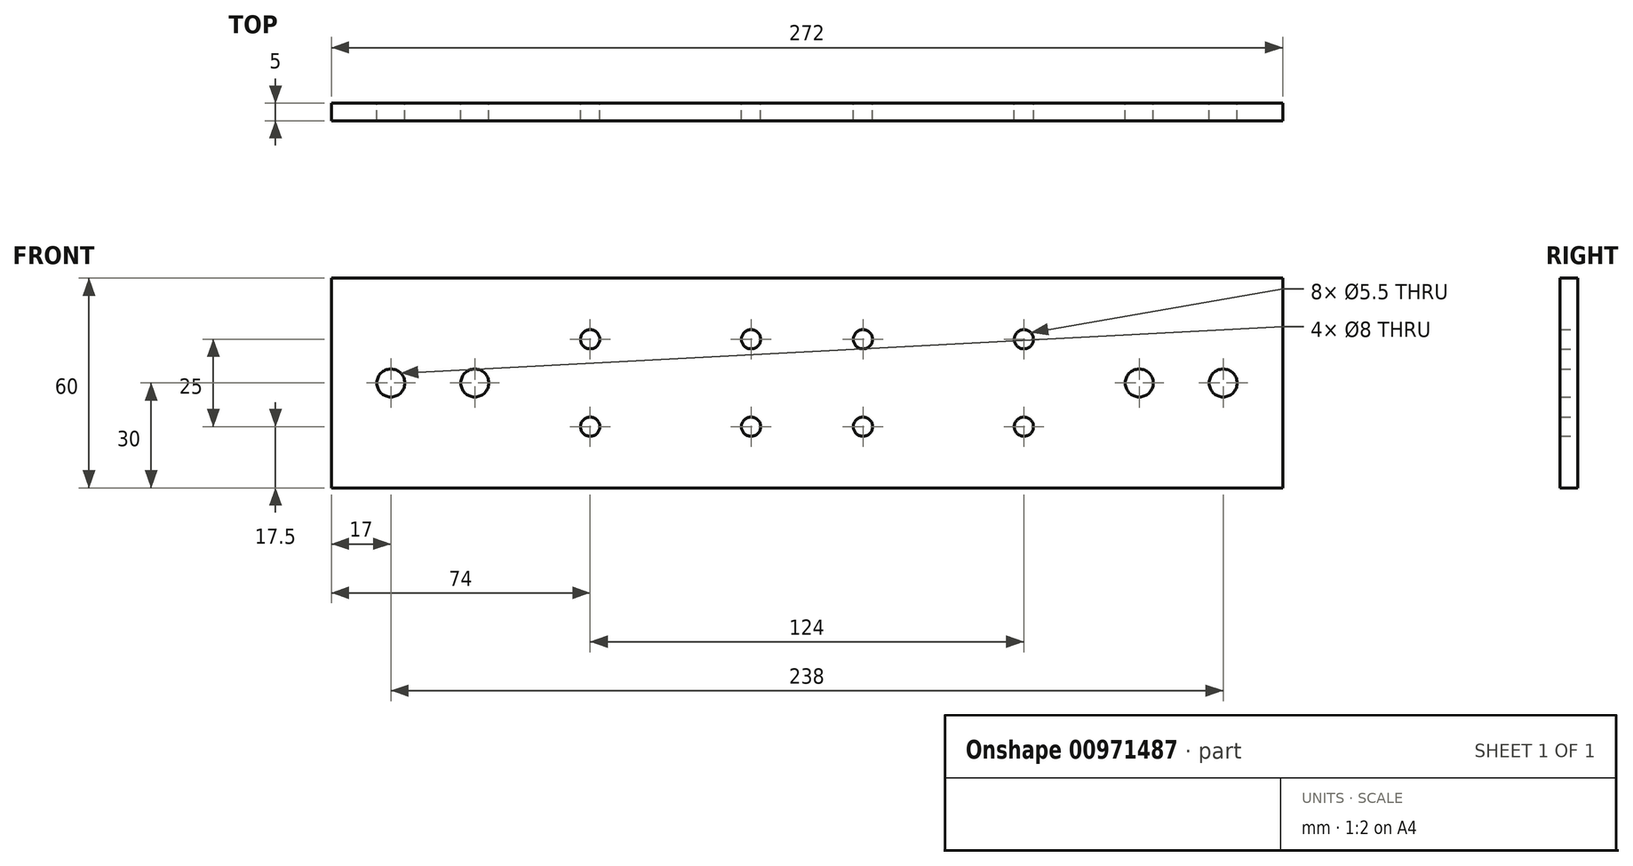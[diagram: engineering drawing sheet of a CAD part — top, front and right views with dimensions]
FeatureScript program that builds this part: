
annotation { "Feature Type Name" : "Feature", "Feature Type Description" : "" }
export const myFeature = defineFeature(function(context is Context, id is Id, definition is map)
    precondition{}
    {
        {
            var Q0;
            Q0=qCreatedBy(makeId("Front.planeOp"),FACE);
            var sketch = newSketch(context, id + "F0", { "sketchPlane" : qUnion([Q0])});
            skLineSegment(sketch, "E0.bottom", {"start": v(136, 30) * mm, "end": v(-136, 30) * mm});
            skLineSegment(sketch, "E0.top", {"start": v(136, -30) * mm, "end": v(-136, -30) * mm});
            skLineSegment(sketch, "E0.left", {"start": v(136, 30) * mm, "end": v(136, -30) * mm});
            skLineSegment(sketch, "E0.right", {"start": v(-136, 30) * mm, "end": v(-136, -30) * mm});
            skPoint(sketch, "E0.middle", {"position": v(0, 0) * mm});
            skPoint(sketch, "E1.orphan", {"position": v(-136, 15) * mm});
            skPoint(sketch, "E2.orphan", {"position": v(-136, -15) * mm});
            skPoint(sketch, "E3.orphan", {"position": v(-126, -30) * mm});
            skPoint(sketch, "E4.orphan", {"position": v(-88, -30) * mm});
            skPoint(sketch, "E5.orphan", {"position": v(88, -30) * mm});
            skPoint(sketch, "E6.orphan", {"position": v(126, -30) * mm});
            skPoint(sketch, "E7.orphan", {"position": v(-10, -30) * mm});
            skPoint(sketch, "E8.orphan", {"position": v(-68, -30) * mm});
            skPoint(sketch, "E9.orphan", {"position": v(68, 30) * mm});
            skPoint(sketch, "E10.orphan", {"position": v(68, -30) * mm});
            skPoint(sketch, "E11.orphan", {"position": v(10, -30) * mm});
            skCircle(sketch, "E12", {"center": v(-119, 0) * mm, "radius": 4 * mm});
            skCircle(sketch, "E13", {"center": v(-95, 0) * mm, "radius": 4 * mm});
            skPoint(sketch, "E14.orphan", {"position": v(-119, 15) * mm});
            skPoint(sketch, "E15.orphan", {"position": v(-95, 15) * mm});
            skPoint(sketch, "E16.orphan", {"position": v(-95, -15) * mm});
            skPoint(sketch, "E17.orphan", {"position": v(-119, -15) * mm});
            skPoint(sketch, "E18.orphan", {"position": v(-88, 0) * mm});
            skPoint(sketch, "E19.orphan", {"position": v(-126, 0) * mm});
            skPoint(sketch, "E20.center.orphan", {"position": v(95, 0) * mm});
            skCircle(sketch, "E21", {"center": v(95, 0) * mm, "radius": 4 * mm});
            skCircle(sketch, "E22", {"center": v(119, 0) * mm, "radius": 4 * mm});
            skPoint(sketch, "E23.orphan", {"position": v(95, 15) * mm});
            skPoint(sketch, "E24.orphan", {"position": v(119, 15) * mm});
            skPoint(sketch, "E25.orphan", {"position": v(126, 0) * mm});
            skPoint(sketch, "E26.orphan", {"position": v(119, -15) * mm});
            skPoint(sketch, "E27.orphan", {"position": v(95, -15) * mm});
            skPoint(sketch, "E28.orphan", {"position": v(88, 0) * mm});
            skCircle(sketch, "E29", {"center": v(-62, 12.5) * mm, "radius": 2.75 * mm});
            skCircle(sketch, "E30", {"center": v(-16, 12.5) * mm, "radius": 2.75 * mm});
            skCircle(sketch, "E31", {"center": v(-62, -12.5) * mm, "radius": 2.75 * mm});
            skCircle(sketch, "E32", {"center": v(-16, -12.5) * mm, "radius": 2.75 * mm});
            skCircle(sketch, "E33", {"center": v(16, 12.5) * mm, "radius": 2.75 * mm});
            skCircle(sketch, "E34", {"center": v(62, 12.5) * mm, "radius": 2.75 * mm});
            skCircle(sketch, "E35", {"center": v(16, -12.5) * mm, "radius": 2.75 * mm});
            skCircle(sketch, "E36", {"center": v(62, -12.5) * mm, "radius": 2.75 * mm});
            skPoint(sketch, "E37.orphan", {"position": v(-62, 20) * mm});
            skPoint(sketch, "E38.orphan", {"position": v(-68, 12.5) * mm});
            skPoint(sketch, "E39.orphan", {"position": v(-16, 20) * mm});
            skPoint(sketch, "E40.orphan", {"position": v(-68, -12.5) * mm});
            skPoint(sketch, "E41.orphan", {"position": v(10, 12.5) * mm});
            skPoint(sketch, "E42.orphan", {"position": v(10, -12.5) * mm});
            skPoint(sketch, "E43.orphan", {"position": v(16, 20) * mm});
            skPoint(sketch, "E44.orphan", {"position": v(62, 20) * mm});
            skPoint(sketch, "E45.trimOffspring.end.orphan", {"position": v(-88, 15) * mm});
            skPoint(sketch, "E46.trimOffspring.end.orphan", {"position": v(-88, -15) * mm});
            skPoint(sketch, "E47.orphan", {"position": v(-126, -15) * mm});
            skPoint(sketch, "E48.start.orphan", {"position": v(-126, 15) * mm});
            skPoint(sketch, "E49.trimOffspring.end.orphan", {"position": v(-10, 20) * mm});
            skPoint(sketch, "E50.trimOffspring.end.orphan", {"position": v(-68, -20) * mm});
            skPoint(sketch, "E51.start.orphan", {"position": v(-68, 20) * mm});
            skPoint(sketch, "E52.end.orphan", {"position": v(68, -20) * mm});
            skPoint(sketch, "E53.trimOffspring.end.orphan", {"position": v(10, -20) * mm});
            skPoint(sketch, "E54.start.orphan", {"position": v(10, 20) * mm});
            skPoint(sketch, "E55.trimOffspring.end.orphan", {"position": v(68, 20) * mm});
            skPoint(sketch, "E56.start.orphan", {"position": v(88, 15) * mm});
            skPoint(sketch, "E57.trimOffspring.end.orphan", {"position": v(126, 15) * mm});
            skPoint(sketch, "E58.start.orphan", {"position": v(126, -15) * mm});
            skPoint(sketch, "E59.trimOffspring.end.orphan", {"position": v(88, -15) * mm});
            skSolve(sketch);
        }
        {
            var Q0;
            Q0=makeQuery(id+"F0.imprint","IMPRINT",FACE,{"disambiguationData":[TD([[makeQuery(id+"F0.imprint","IMPRINT",EDGE,{"derivedFrom":sQuery(id+"F0.wireOp",EDGE,"E0.bottom")}),1.0]])]});
            extrude(context, id + "F1", {"entities" : qUnion([Q0]), "depth" : 5 * mm, "offsetDistance" : 25 * mm});
        }
    });
